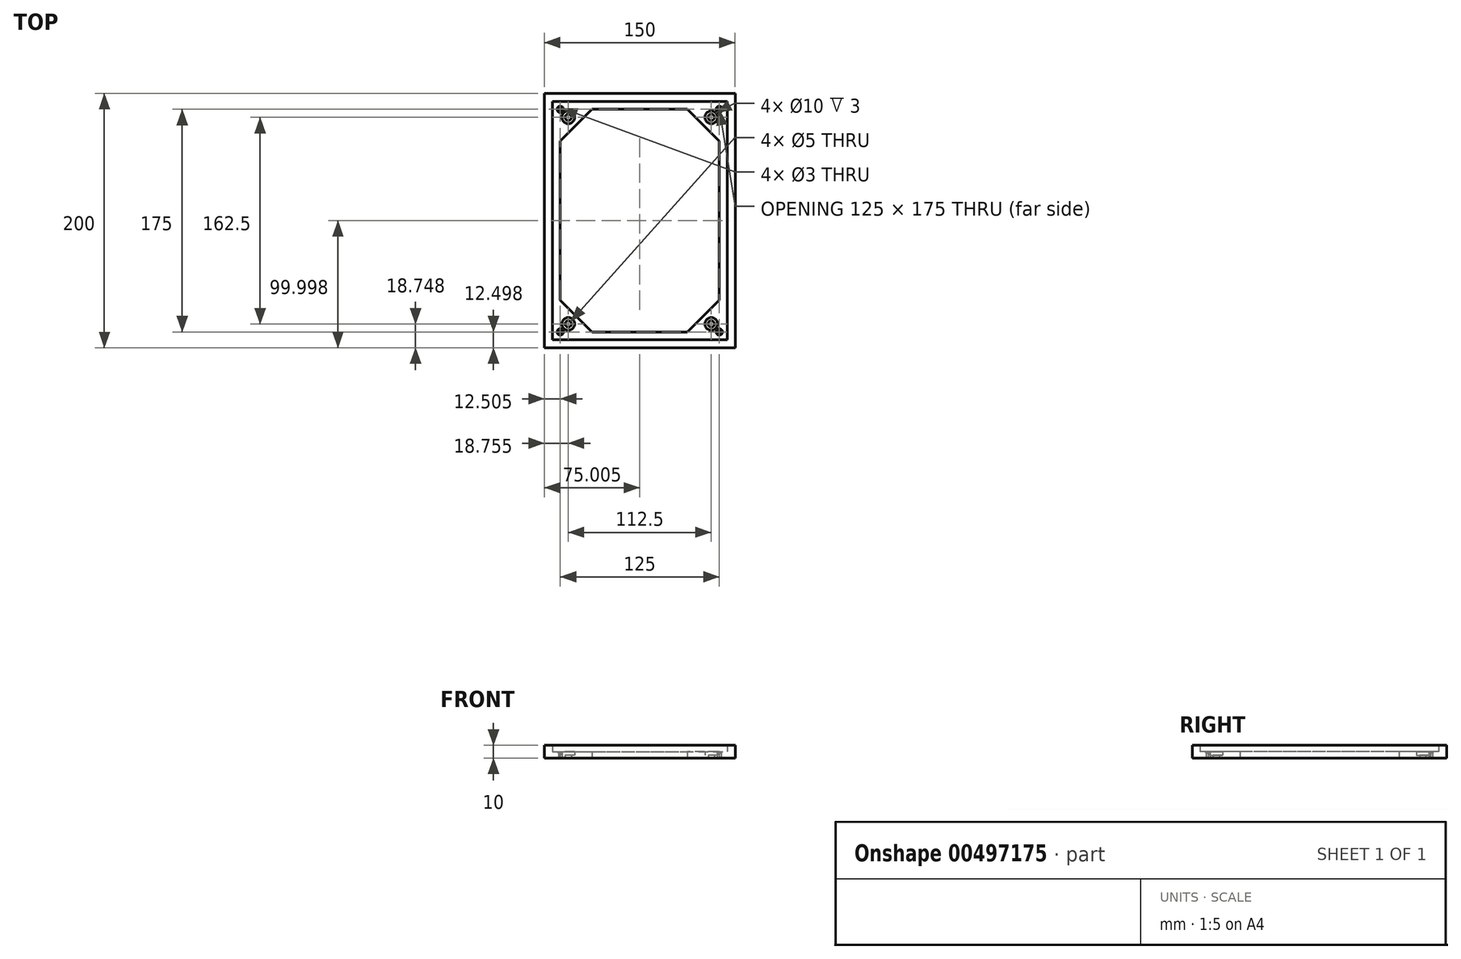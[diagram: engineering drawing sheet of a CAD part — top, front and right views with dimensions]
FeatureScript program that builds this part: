
annotation { "Feature Type Name" : "Feature", "Feature Type Description" : "" }
export const myFeature = defineFeature(function(context is Context, id is Id, definition is map)
    precondition{}
    {
        {
            var Q0;
            Q0=qCreatedBy(makeId("Top.planeOp"),FACE);
            var sketch = newSketch(context, id + "F0", { "sketchPlane" : qUnion([Q0])});
            skLineSegment(sketch, "E0.bottom", {"start": v(-75.03, 100) * mm, "end": v(74.97, 100) * mm});
            skLineSegment(sketch, "E0.top", {"start": v(-75.03, -100) * mm, "end": v(74.97, -100) * mm});
            skLineSegment(sketch, "E0.left", {"start": v(-75.03, 100) * mm, "end": v(-75.03, -100) * mm});
            skLineSegment(sketch, "E0.right", {"start": v(74.97, 100) * mm, "end": v(74.97, -100) * mm});
            skLineSegment(sketch, "E1.bottom", {"start": v(-68.78, 93.76) * mm, "end": v(68.72, 93.76) * mm});
            skLineSegment(sketch, "E1.top", {"start": v(-68.78, -93.74) * mm, "end": v(68.72, -93.74) * mm});
            skLineSegment(sketch, "E1.left", {"start": v(-68.78, 93.76) * mm, "end": v(-68.78, -93.74) * mm});
            skLineSegment(sketch, "E1.right", {"start": v(68.72, 93.76) * mm, "end": v(68.72, -93.74) * mm});
            skLineSegment(sketch, "E2.bottom", {"start": v(-62.53, 87.5) * mm, "end": v(62.47, 87.5) * mm});
            skLineSegment(sketch, "E2.top", {"start": v(-62.53, -87.5) * mm, "end": v(62.47, -87.5) * mm});
            skLineSegment(sketch, "E2.left", {"start": v(-62.53, 87.5) * mm, "end": v(-62.53, -87.5) * mm});
            skLineSegment(sketch, "E2.right", {"start": v(62.47, 87.5) * mm, "end": v(62.47, -87.5) * mm});
            skPoint(sketch, "E3", {"position": v(37.47, 87.5) * mm});
            skPoint(sketch, "E4", {"position": v(37.47, -87.5) * mm});
            skPoint(sketch, "E5", {"position": v(-37.53, 87.5) * mm});
            skPoint(sketch, "E6", {"position": v(-37.53, -87.5) * mm});
            skPoint(sketch, "E7", {"position": v(-62.53, 62.5) * mm});
            skPoint(sketch, "E8", {"position": v(62.47, 62.5) * mm});
            skPoint(sketch, "E9", {"position": v(62.47, -62.5) * mm});
            skPoint(sketch, "E10", {"position": v(-62.53, -62.5) * mm});
            skPoint(sketch, "E11", {"position": v(-62.53, 87.5) * mm});
            skPoint(sketch, "E12", {"position": v(62.47, 87.5) * mm});
            skPoint(sketch, "E13", {"position": v(62.47, -87.5) * mm});
            skPoint(sketch, "E14", {"position": v(-62.53, -87.5) * mm});
            skLineSegment(sketch, "E15", {"start": v(-62.53, -62.5) * mm, "end": v(-37.53, -87.5) * mm});
            skLineSegment(sketch, "E16", {"start": v(37.47, -87.5) * mm, "end": v(62.47, -62.5) * mm});
            skLineSegment(sketch, "E17", {"start": v(62.47, 62.5) * mm, "end": v(37.47, 87.5) * mm});
            skLineSegment(sketch, "E18", {"start": v(-37.53, 87.5) * mm, "end": v(-62.53, 62.5) * mm});
            skPoint(sketch, "E19", {"position": v(-50.03, 75) * mm});
            skPoint(sketch, "E20", {"position": v(49.97, 75) * mm});
            skPoint(sketch, "E21", {"position": v(49.97, -75) * mm});
            skPoint(sketch, "E22", {"position": v(-50.03, -75) * mm});
            skLineSegment(sketch, "E23", {"start": v(-62.53, 87.5) * mm, "end": v(-50.03, 75) * mm, "construction": true});
            skLineSegment(sketch, "E24", {"start": v(62.47, 87.5) * mm, "end": v(49.97, 75) * mm, "construction": true});
            skLineSegment(sketch, "E25", {"start": v(62.47, -87.5) * mm, "end": v(49.97, -75) * mm, "construction": true});
            skLineSegment(sketch, "E26", {"start": v(-62.53, -87.5) * mm, "end": v(-50.03, -75) * mm, "construction": true});
            skPoint(sketch, "E27", {"position": v(-56.28, 81.26) * mm});
            skPoint(sketch, "E28", {"position": v(56.22, 81.26) * mm});
            skPoint(sketch, "E29", {"position": v(56.22, -81.24) * mm});
            skPoint(sketch, "E30", {"position": v(-56.28, -81.24) * mm});
            skCircle(sketch, "E31", {"center": v(-56.28, -81.24) * mm, "radius": 2.5 * mm});
            skCircle(sketch, "E32", {"center": v(56.22, -81.24) * mm, "radius": 2.5 * mm});
            skCircle(sketch, "E33", {"center": v(56.22, 81.26) * mm, "radius": 2.5 * mm});
            skCircle(sketch, "E34", {"center": v(-56.28, 81.26) * mm, "radius": 2.5 * mm});
            skCircle(sketch, "E35", {"center": v(-56.28, 81.26) * mm, "radius": 5 * mm});
            skCircle(sketch, "E36", {"center": v(56.22, 81.26) * mm, "radius": 5 * mm});
            skCircle(sketch, "E37", {"center": v(-56.28, -81.24) * mm, "radius": 5 * mm});
            skCircle(sketch, "E38", {"center": v(56.22, -81.24) * mm, "radius": 5 * mm});
            skSolve(sketch);
        }
        {
            var Q0;
            Q0=makeQuery(id+"F0.imprint","IMPRINT",FACE,{"disambiguationData":[TD([[makeQuery(id+"F0.imprint","IMPRINT",EDGE,{"derivedFrom":sQuery(id+"F0.wireOp",EDGE,"E0.bottom")}),-1.0]])]});
            extrude(context, id + "F1", {"entities" : qUnion([Q0]), "depth" : 10 * mm});
        }
        {
            var Q0;
            Q0=makeQuery(id+"F0.imprint","IMPRINT",FACE,{"disambiguationData":[TD([[makeQuery(id+"F0.imprint","IMPRINT",EDGE,{"derivedFrom":sQuery(id+"F0.wireOp",EDGE,"E1.bottom")}),-1.0]])]});
            var Q1;
            {var subQ5=sQuery(id+"F0.wireOp",EDGE,"E18");Q1=makeQuery(id+"F0.imprint","IMPRINT",FACE,{"disambiguationData":[TD([[makeQuery(id+"F0.imprint","IMPRINT",EDGE,{"derivedFrom":subQ5}),-1.0]])]});}
            var Q2;
            {var subQ0=sQuery(id+"F0.wireOp",EDGE,"E17");Q2=makeQuery(id+"F0.imprint","IMPRINT",FACE,{"disambiguationData":[TD([[makeQuery(id+"F0.imprint","IMPRINT",EDGE,{"derivedFrom":subQ0}),-1.0]])]});}
            var Q3;
            {var subQ0=sQuery(id+"F0.wireOp",EDGE,"E16");Q3=makeQuery(id+"F0.imprint","IMPRINT",FACE,{"disambiguationData":[TD([[makeQuery(id+"F0.imprint","IMPRINT",EDGE,{"derivedFrom":subQ0}),-1.0]])]});}
            var Q4;
            {var subQ5=sQuery(id+"F0.wireOp",EDGE,"E15");Q4=makeQuery(id+"F0.imprint","IMPRINT",FACE,{"disambiguationData":[TD([[makeQuery(id+"F0.imprint","IMPRINT",EDGE,{"derivedFrom":subQ5}),-1.0]])]});}
            extrude(context, id + "F2", {"entities" : qUnion([Q0, Q1, Q2, Q3, Q4]), "operationType" : NewBodyOperationType.ADD, "depth" : 5 * mm, "offsetDistance" : 25 * mm});
        }
        {
            var Q0;
            Q0=makeQuery(id+"F0.imprint","IMPRINT",FACE,{"disambiguationData":[TD([[makeQuery(id+"F0.imprint","IMPRINT",EDGE,{"derivedFrom":sQuery(id+"F0.wireOp",EDGE,"E34")}),-1.0]])]});
            var Q1;
            Q1=makeQuery(id+"F0.imprint","IMPRINT",FACE,{"disambiguationData":[TD([[makeQuery(id+"F0.imprint","IMPRINT",EDGE,{"derivedFrom":sQuery(id+"F0.wireOp",EDGE,"E33")}),-1.0]])]});
            var Q2;
            Q2=makeQuery(id+"F0.imprint","IMPRINT",FACE,{"disambiguationData":[TD([[makeQuery(id+"F0.imprint","IMPRINT",EDGE,{"derivedFrom":sQuery(id+"F0.wireOp",EDGE,"E32")}),-1.0]])]});
            var Q3;
            Q3=makeQuery(id+"F0.imprint","IMPRINT",FACE,{"disambiguationData":[TD([[makeQuery(id+"F0.imprint","IMPRINT",EDGE,{"derivedFrom":sQuery(id+"F0.wireOp",EDGE,"E31")}),-1.0]])]});
            extrude(context, id + "F3", {"entities" : qUnion([Q0, Q1, Q2, Q3]), "operationType" : NewBodyOperationType.ADD, "depth" : 2 * mm});
        }
        {
            var Q0;
            Q0=makeQuery(id+"F2.opExtrude","CAP_FACE",FACE,{"disambiguationData":[OSD([sQuery(id+"F0.wireOp",EDGE,"E1.bottom"),sQuery(id+"F0.wireOp",EDGE,"E1.top"),sQuery(id+"F0.wireOp",EDGE,"E1.left"),sQuery(id+"F0.wireOp",EDGE,"E1.right"),sQuery(id+"F0.wireOp",EDGE,"E2.bottom"),sQuery(id+"F0.wireOp",EDGE,"E2.top"),sQuery(id+"F0.wireOp",EDGE,"E2.left"),sQuery(id+"F0.wireOp",EDGE,"E2.right"),sQuery(id+"F0.wireOp",EDGE,"E15"),sQuery(id+"F0.wireOp",EDGE,"E16"),sQuery(id+"F0.wireOp",EDGE,"E17"),sQuery(id+"F0.wireOp",EDGE,"E18"),sQuery(id+"F0.wireOp",EDGE,"E35"),sQuery(id+"F0.wireOp",EDGE,"E36"),sQuery(id+"F0.wireOp",EDGE,"E37"),sQuery(id+"F0.wireOp",EDGE,"E38")])],"isStart":false});
            var sketch = newSketch(context, id + "F4", { "sketchPlane" : qUnion([Q0])});
            skPoint(sketch, "E39", {"position": v(-62.53, 87.5) * mm});
            skPoint(sketch, "E40", {"position": v(62.47, 87.5) * mm});
            skPoint(sketch, "E41", {"position": v(62.47, -87.5) * mm});
            skPoint(sketch, "E42", {"position": v(-62.53, -87.5) * mm});
            skSolve(sketch);
        }
        {
            var Q0;
            Q0=sQuery(id+"F4.wireOp",VERTEX,"E39");
            var Q1;
            Q1=sQuery(id+"F4.wireOp",VERTEX,"E40");
            var Q2;
            Q2=sQuery(id+"F4.wireOp",VERTEX,"E41");
            var Q3;
            Q3=sQuery(id+"F4.wireOp",VERTEX,"E42");
            var Q4;
            Q4=makeQuery(id+"F1.opExtrude","SWEPT_BODY",BODY,{"disambiguationData":[OSD([sQuery(id+"F0.wireOp",EDGE,"E0.bottom"),sQuery(id+"F0.wireOp",EDGE,"E0.top"),sQuery(id+"F0.wireOp",EDGE,"E0.left"),sQuery(id+"F0.wireOp",EDGE,"E0.right"),sQuery(id+"F0.wireOp",EDGE,"E1.bottom"),sQuery(id+"F0.wireOp",EDGE,"E1.top"),sQuery(id+"F0.wireOp",EDGE,"E1.left"),sQuery(id+"F0.wireOp",EDGE,"E1.right")])]});
            hole(context, id + "F5", {"style" : HoleStyle.C_SINK, "endStyle" : HoleEndStyle.THROUGH, "holeDiameter" : 3 * mm, "cSinkDiameter" : 5 * mm, "cSinkAngle" : 90 * degree, "isTappedThrough" : true, "tappedDepth" : 12 * mm, "tapClearance" : 3, "locations" : qUnion([Q0, Q1, Q2, Q3]), "scope" : qUnion([Q4])});
        }
    });
